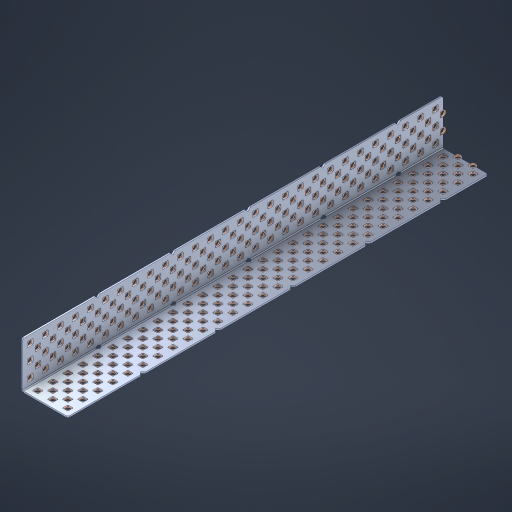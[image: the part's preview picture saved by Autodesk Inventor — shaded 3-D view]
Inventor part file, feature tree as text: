
AUTODESK INVENTOR PART (.ipt)
format: ipt  version: 2023 (Build 270158000, 158)  size: 2,856,960 bytes
history: native  units: in
note: dims shown in document units (in); Inventor stores cm internally (conversion verified against a paired STEP export)
features: other x286, extrude x278, sheet_metal_op x8, sketch x7, pattern_linear x3, mirror x1, chamfer x1
ambient origin geometry x8: Origin, YZ Plane, XZ Plane, XY Plane, X Axis, Y Axis, Z Axis, Center Point
bodies: Solid1 (feature_tree), Body (feature_tree)
feature tree (584):
  sheet_metal_op  "Flanges"
  sheet_metal_op  "Body Pattern"
  pattern_linear  "Center Double"  Spacing1=1.5in  [1 undecoded]
  pattern_linear  "Center Pattern"  Spacing1=0.1875in  [1 undecoded]
  other  "Arc Length"
  pattern_linear  "Notch Pattern"  Spacing1=0.0469in  [1 undecoded]
  other  "Diagonal Plane"
  mirror  "Everything Mirrored"
  chamfer  "End Chamfer"
  sketch  "Sketch1"  dims[d0=1.5in]
  other  "Plate1"
  sketch  "Sketch2"  dims[d1=14.0in]
  other  "Plate2"
  sheet_metal_op  "Bend1"
  sheet_metal_op  "Corner1"
  sketch  "Sketch8"  dims[d2=0.0469in]
  sketch  "Sketch9"  dims[d3=0.0469in]
  other  "Srf91"
  sheet_metal_op  "Body Pattern Sketch"
  other  "Srf92"
  sketch  "Sketch13"  dims[d4=0.0234in]
  sketch  "Sketch15"  dims[d5=0.0938in]
  sketch  "Sketch16"  dims[d6=0.0469in d7=1.5in d8=90.0deg d9=0.0312in d10=0.1875in d11=0.0469in d12=0.0469in d49=0.182in d50=0.02in d52=0.25in d53=0.0469in d54=0.0in d55=0.172in d56=1.0in d57=0.0in d85=0.1473in d86=0.1659in d89=0.0469in d90=0.0in d91=0.04in d92=0.0491in d95=2.5in d96=0.04in d97=0.25in d98=45.0deg d106=0.182in d107=0.02in d110=0.0469in d111=0.0in d112=0.172in d113=0.5in d114=0.0in d117=0.5in d126=0.0491in d127=0.1227in d128=0.08in d129=0.04in d130=2.5in d131=0.25in d132=11.0236in d134=0.5in d135=1.1811in d137=0.5in d140=0.5in d141=1.0in d142=0.3937in d144=0.5in d145=0.071in d146=0.7874in d148=0.5in]
  other  "Srf786"
  other  "Srf856"
  other  "Srf889"
  other  "Srf890"
  other  "Srf891"
  other  "Srf1275"
  other  "Srf1276"
  other  "Srf1278"
  other  "Srf1277"
  other  "Srf1285"
  other  "Srf1286"
  other  "Srf1287"
  other  "Srf1445"
  other  "Srf1446"
  other  "Srf1447"
  other  "Srf1448"
  other  "Srf1449"
  other  "Srf1537"
  other  "Srf1538"
  other  "Srf1539"
  other  "Srf1540"
  other  "Srf1541"
  other  "Srf1807"
  other  "Srf1808"
  other  "Srf1809"
  other  "Srf1810"
  other  "Srf1811"
  other  "Srf1812"
  other  "Srf1813"
  other  "Srf1814"
  other  "Srf1815"
  other  "Srf1816"
  other  "Srf1817"
  other  "Srf1818"
  other  "Srf1819"
  other  "Srf1820"
  other  "Srf1821"
  other  "Srf1822"
  other  "Srf1823"
  other  "Srf1824"
  other  "Srf1825"
  other  "Srf1959"
  other  "Srf1960"
  other  "Srf1961"
  other  "Srf1962"
  other  "Srf1963"
  other  "Srf1964"
  other  "Srf1965"
  other  "Srf1966"
  other  "Srf1967"
  other  "Srf1968"
  other  "Srf1969"
  other  "Srf1970"
  other  "Srf1971"
  other  "Srf1972"
  other  "Srf1973"
  other  "Srf1974"
  other  "Srf1975"
  other  "Srf1976"
  other  "Srf1977"
  other  "Srf2009"
  other  "Srf2010"
  other  "Srf2011"
  other  "Srf2012"
  other  "Srf2013"
  other  "Srf2014"
  other  "Srf2015"
  other  "Srf2016"
  other  "Srf2017"
  other  "Srf2018"
  other  "Srf2019"
  other  "Srf2020"
  other  "Srf2021"
  other  "Srf2022"
  other  "Srf2023"
  other  "Srf2024"
  other  "Srf2025"
  other  "Srf2026"
  other  "Srf2027"
  other  "Srf2028"
  other  "Srf2029"
  other  "Srf2030"
  other  "Srf2031"
  other  "Srf2032"
  other  "Srf2033"
  other  "Srf2034"
  other  "Srf2035"
  other  "Srf2036"
  other  "Srf2043"
  other  "Srf2044"
  other  "Srf2045"
  other  "Srf2046"
  other  "Srf2047"
  other  "Srf2048"
  other  "Srf2049"
  other  "Srf2050"
  other  "Srf2051"
  other  "Srf2052"
  other  "Srf2053"
  other  "Srf2054"
  other  "Srf2055"
  other  "Srf2056"
  other  "Srf2057"
  other  "Srf2058"
  other  "Srf2059"
  other  "Srf2060"
  other  "Srf2061"
  other  "Srf2062"
  other  "Srf2063"
  other  "Srf2064"
  other  "Srf2065"
  other  "Srf2066"
  other  "Srf2067"
  other  "Srf2068"
  other  "Srf2069"
  other  "Srf2076"
  other  "Srf2077"
  other  "Srf2078"
  other  "Srf2079"
  other  "Srf2080"
  other  "Srf2081"
  other  "Srf2082"
  other  "Srf2083"
  other  "Srf2084"
  other  "Srf2085"
  other  "Srf2086"
  other  "Srf2087"
  other  "Srf2088"
  other  "Srf2089"
  other  "Srf2090"
  other  "Srf2091"
  other  "Srf2092"
  other  "Srf2093"
  other  "Srf2094"
  other  "Srf2095"
  other  "Srf2096"
  other  "Srf2097"
  other  "Srf2098"
  other  "Srf2099"
  other  "Srf2100"
  other  "Srf2101"
  other  "Srf2102"
  other  "Srf2103"
  other  "Srf2104"
  other  "Srf2105"
  other  "Srf2106"
  other  "Srf2107"
  other  "Srf2108"
  other  "Srf2109"
  other  "Srf2110"
  other  "Srf2111"
  other  "Srf2112"
  other  "Srf2113"
  other  "Srf2114"
  other  "Srf2115"
  other  "Srf2116"
  other  "Srf2117"
  other  "Srf2118"
  other  "Srf2119"
  other  "Srf2120"
  other  "Srf2121"
  other  "Srf2122"
  other  "Srf2123"
  other  "Srf2124"
  other  "Srf2125"
  other  "Srf2126"
  other  "Srf2127"
  other  "Srf2128"
  other  "Srf2129"
  other  "Srf2130"
  other  "Srf2131"
  other  "Srf2132"
  other  "Srf2133"
  other  "Srf2134"
  other  "Srf2135"
  other  "Srf2136"
  other  "Srf2137"
  other  "Srf2138"
  other  "Srf2139"
  other  "Srf2140"
  other  "Srf2141"
  other  "Srf2142"
  other  "Srf2143"
  other  "Srf2144"
  other  "Srf2145"
  other  "Srf2146"
  other  "Srf2147"
  other  "Srf2148"
  other  "Srf2149"
  other  "Srf2150"
  other  "Srf2151"
  other  "Srf2152"
  other  "Srf2153"
  other  "Srf2154"
  other  "Srf2155"
  other  "Srf2156"
  other  "Srf2157"
  other  "Srf2179"
  other  "Srf2180"
  other  "Srf2181"
  other  "Srf2182"
  other  "Srf2183"
  other  "Srf2184"
  other  "Srf2185"
  other  "Srf2186"
  other  "Srf2187"
  other  "Srf2188"
  other  "Srf2189"
  other  "Srf2190"
  other  "Srf2191"
  other  "Srf2192"
  other  "Srf2193"
  other  "Srf2194"
  other  "Srf2195"
  other  "Srf2196"
  other  "Srf2197"
  other  "Srf2198"
  other  "Srf2199"
  other  "Srf2200"
  other  "Srf2201"
  other  "Srf2202"
  other  "Srf2203"
  other  "Srf2204"
  other  "Srf2205"
  other  "Srf2206"
  other  "Srf2207"
  other  "Srf2208"
  other  "Srf2209"
  other  "Srf2210"
  other  "Srf2211"
  other  "Srf2212"
  other  "Srf2213"
  other  "Srf2214"
  other  "Srf2215"
  other  "Srf2216"
  other  "Srf2217"
  other  "Srf2218"
  other  "Srf2219"
  other  "Srf2220"
  other  "Srf2221"
  other  "Srf2222"
  other  "Srf2223"
  other  "Srf2224"
  other  "Srf2225"
  other  "Srf2226"
  other  "Srf2227"
  other  "Srf2228"
  other  "Srf2229"
  other  "Srf2230"
  other  "Srf2231"
  other  "Srf2232"
  other  "Srf2233"
  other  "Srf2234"
  other  "Srf2235"
  other  "Srf2236"
  other  "Srf2237"
  other  "Srf2238"
  other  "Srf2239"
  other  "Srf2240"
  other  "Srf2241"
  other  "Srf2242"
  other  "Srf2243"
  other  "Srf2244"
  other  "Srf2245"
  other  "Srf2246"
  other  "Srf2247"
  other  "Srf2248"
  other  "Srf2249"
  other  "Srf2250"
  other  "Srf2251"
  other  "Srf2252"
  other  "Srf2253"
  other  "Srf2254"
  other  "Srf2255"
  other  "Srf2256"
  other  "Srf2257"
  other  "Srf2258"
  other  "Srf2259"
  sheet_metal_op  "Body Stamp"
  sheet_metal_op  "Body Circle"
  other  "Center Stamp"
  other  "Center Circle"
  sheet_metal_op  "Notch"
  extrude  "ExtrusionSrf92"  Depth=0.0469in
  extrude  "ExtrusionSrf856"  Depth=0.182in
  extrude  "ExtrusionSrf889"  Depth=0.02in
  extrude  "ExtrusionSrf890"  Depth=0.25in
  extrude  "ExtrusionSrf891"  Depth=0.0469in
  extrude  "ExtrusionSrf1275"  TaperAngle=0.0deg  [1 undecoded]
  extrude  "ExtrusionSrf1276"  Depth=0.5in
  extrude  "ExtrusionSrf1277"  Depth=1.0in TaperAngle=0.0deg
  extrude  "ExtrusionSrf1345"  Depth=0.5in
  extrude  "ExtrusionSrf1346"  Depth=0.5in
  extrude  "ExtrusionSrf1347"  Depth=0.0469in
  extrude  "ExtrusionSrf1348"  Depth=0.5in TaperAngle=0.0deg
  extrude  "ExtrusionSrf1445"  Depth=0.5in
  extrude  "ExtrusionSrf1446"  Depth=0.25in TaperAngle=45.0deg
  extrude  "ExtrusionSrf1447"  Depth=0.182in
  extrude  "ExtrusionSrf1448"  Depth=0.02in
  extrude  "ExtrusionSrf1449"  Depth=0.0469in
  extrude  "ExtrusionSrf1537"  TaperAngle=0.0deg  [1 undecoded]
  extrude  "ExtrusionSrf1538"  Depth=0.5in
  extrude  "ExtrusionSrf1539"  Depth=0.5in TaperAngle=0.0deg
  extrude  "ExtrusionSrf1540"  Depth=0.5in
  extrude  "ExtrusionSrf1541"  Depth=0.5in
  extrude  "ExtrusionSrf1807"  Depth=0.5in
  extrude  "ExtrusionSrf1808"  Depth=0.5in
  extrude  "ExtrusionSrf1809"  Depth=0.5in
  extrude  "ExtrusionSrf1810"  Depth=0.5in
  extrude  "ExtrusionSrf1811"  Depth=0.25in
  extrude  "ExtrusionSrf1812"  Depth=0.5in
  extrude  "ExtrusionSrf1813"  Depth=0.5in
  extrude  "ExtrusionSrf1814"  Depth=0.5in
  extrude  "ExtrusionSrf1815"  Depth=1.0in
  extrude  "ExtrusionSrf1816"  Depth=0.3937in
  extrude  "ExtrusionSrf1817"  Depth=0.5in
  extrude  "ExtrusionSrf1818"  Depth=0.5in
  extrude  "ExtrusionSrf1819"  [1 undecoded]
  extrude  "ExtrusionSrf1820"  [1 undecoded]
  extrude  "ExtrusionSrf1821"  [1 undecoded]
  extrude  "ExtrusionSrf1822"  [1 undecoded]
  extrude  "ExtrusionSrf1823"  [1 undecoded]
  extrude  "ExtrusionSrf1824"  [1 undecoded]
  extrude  "ExtrusionSrf1825"  [1 undecoded]
  extrude  "ExtrusionSrf1959"  [1 undecoded]
  extrude  "ExtrusionSrf1960"  [1 undecoded]
  extrude  "ExtrusionSrf1961"  [1 undecoded]
  extrude  "ExtrusionSrf1962"  [1 undecoded]
  extrude  "ExtrusionSrf1963"  [1 undecoded]
  extrude  "ExtrusionSrf1964"  [1 undecoded]
  extrude  "ExtrusionSrf1965"  [1 undecoded]
  extrude  "ExtrusionSrf1966"  [1 undecoded]
  extrude  "ExtrusionSrf1967"  [1 undecoded]
  extrude  "ExtrusionSrf1968"  [1 undecoded]
  extrude  "ExtrusionSrf1969"  [1 undecoded]
  extrude  "ExtrusionSrf1970"  [1 undecoded]
  extrude  "ExtrusionSrf1971"  [1 undecoded]
  extrude  "ExtrusionSrf1972"  [1 undecoded]
  extrude  "ExtrusionSrf1973"  [1 undecoded]
  extrude  "ExtrusionSrf1974"  [1 undecoded]
  extrude  "ExtrusionSrf1975"  [1 undecoded]
  extrude  "ExtrusionSrf1976"  [1 undecoded]
  extrude  "ExtrusionSrf1977"  [1 undecoded]
  extrude  "ExtrusionSrf2009"  [1 undecoded]
  extrude  "ExtrusionSrf2010"  [1 undecoded]
  extrude  "ExtrusionSrf2011"  [1 undecoded]
  extrude  "ExtrusionSrf2012"  [1 undecoded]
  extrude  "ExtrusionSrf2013"  [1 undecoded]
  extrude  "ExtrusionSrf2014"  [1 undecoded]
  extrude  "ExtrusionSrf2015"  [1 undecoded]
  extrude  "ExtrusionSrf2016"  [1 undecoded]
  extrude  "ExtrusionSrf2017"  [1 undecoded]
  extrude  "ExtrusionSrf2018"  [1 undecoded]
  extrude  "ExtrusionSrf2019"  [1 undecoded]
  extrude  "ExtrusionSrf2020"  [1 undecoded]
  extrude  "ExtrusionSrf2021"  [1 undecoded]
  extrude  "ExtrusionSrf2022"  [1 undecoded]
  extrude  "ExtrusionSrf2023"  [1 undecoded]
  extrude  "ExtrusionSrf2024"  [1 undecoded]
  extrude  "ExtrusionSrf2025"  [1 undecoded]
  extrude  "ExtrusionSrf2026"  [1 undecoded]
  extrude  "ExtrusionSrf2027"  [1 undecoded]
  extrude  "ExtrusionSrf2028"  [1 undecoded]
  extrude  "ExtrusionSrf2029"  [1 undecoded]
  extrude  "ExtrusionSrf2030"  [1 undecoded]
  extrude  "ExtrusionSrf2031"  [1 undecoded]
  extrude  "ExtrusionSrf2032"  [1 undecoded]
  extrude  "ExtrusionSrf2033"  [1 undecoded]
  extrude  "ExtrusionSrf2034"  [1 undecoded]
  extrude  "ExtrusionSrf2035"  [1 undecoded]
  extrude  "ExtrusionSrf2036"  [1 undecoded]
  extrude  "ExtrusionSrf2043"  [1 undecoded]
  extrude  "ExtrusionSrf2044"  [1 undecoded]
  extrude  "ExtrusionSrf2045"  [1 undecoded]
  extrude  "ExtrusionSrf2046"  [1 undecoded]
  extrude  "ExtrusionSrf2047"  [1 undecoded]
  extrude  "ExtrusionSrf2048"  [1 undecoded]
  extrude  "ExtrusionSrf2049"  [1 undecoded]
  extrude  "ExtrusionSrf2050"  [1 undecoded]
  extrude  "ExtrusionSrf2051"  [1 undecoded]
  extrude  "ExtrusionSrf2052"  [1 undecoded]
  extrude  "ExtrusionSrf2053"  [1 undecoded]
  extrude  "ExtrusionSrf2054"  [1 undecoded]
  extrude  "ExtrusionSrf2055"  [1 undecoded]
  extrude  "ExtrusionSrf2056"  [1 undecoded]
  extrude  "ExtrusionSrf2057"  [1 undecoded]
  extrude  "ExtrusionSrf2058"  [1 undecoded]
  extrude  "ExtrusionSrf2059"  [1 undecoded]
  extrude  "ExtrusionSrf2060"  [1 undecoded]
  extrude  "ExtrusionSrf2061"  [1 undecoded]
  extrude  "ExtrusionSrf2062"  [1 undecoded]
  extrude  "ExtrusionSrf2063"  [1 undecoded]
  extrude  "ExtrusionSrf2064"  [1 undecoded]
  extrude  "ExtrusionSrf2065"  [1 undecoded]
  extrude  "ExtrusionSrf2066"  [1 undecoded]
  extrude  "ExtrusionSrf2067"  [1 undecoded]
  extrude  "ExtrusionSrf2068"  [1 undecoded]
  extrude  "ExtrusionSrf2069"  [1 undecoded]
  extrude  "ExtrusionSrf2076"  [1 undecoded]
  extrude  "ExtrusionSrf2077"  [1 undecoded]
  extrude  "ExtrusionSrf2078"  [1 undecoded]
  extrude  "ExtrusionSrf2079"  [1 undecoded]
  extrude  "ExtrusionSrf2080"  [1 undecoded]
  extrude  "ExtrusionSrf2081"  [1 undecoded]
  extrude  "ExtrusionSrf2082"  [1 undecoded]
  extrude  "ExtrusionSrf2083"  [1 undecoded]
  extrude  "ExtrusionSrf2084"  [1 undecoded]
  extrude  "ExtrusionSrf2085"  [1 undecoded]
  extrude  "ExtrusionSrf2086"  [1 undecoded]
  extrude  "ExtrusionSrf2087"  [1 undecoded]
  extrude  "ExtrusionSrf2088"  [1 undecoded]
  extrude  "ExtrusionSrf2089"  [1 undecoded]
  extrude  "ExtrusionSrf2090"  [1 undecoded]
  extrude  "ExtrusionSrf2091"  [1 undecoded]
  extrude  "ExtrusionSrf2092"  [1 undecoded]
  extrude  "ExtrusionSrf2093"  [1 undecoded]
  extrude  "ExtrusionSrf2094"  [1 undecoded]
  extrude  "ExtrusionSrf2095"  [1 undecoded]
  extrude  "ExtrusionSrf2096"  [1 undecoded]
  extrude  "ExtrusionSrf2097"  [1 undecoded]
  extrude  "ExtrusionSrf2098"  [1 undecoded]
  extrude  "ExtrusionSrf2099"  [1 undecoded]
  extrude  "ExtrusionSrf2100"  [1 undecoded]
  extrude  "ExtrusionSrf2101"  [1 undecoded]
  extrude  "ExtrusionSrf2102"  [1 undecoded]
  extrude  "ExtrusionSrf2103"  [1 undecoded]
  extrude  "ExtrusionSrf2104"  [1 undecoded]
  extrude  "ExtrusionSrf2105"  [1 undecoded]
  extrude  "ExtrusionSrf2106"  [1 undecoded]
  extrude  "ExtrusionSrf2107"  [1 undecoded]
  extrude  "ExtrusionSrf2108"  [1 undecoded]
  extrude  "ExtrusionSrf2109"  [1 undecoded]
  extrude  "ExtrusionSrf2110"  [1 undecoded]
  extrude  "ExtrusionSrf2111"  [1 undecoded]
  extrude  "ExtrusionSrf2112"  [1 undecoded]
  extrude  "ExtrusionSrf2113"  [1 undecoded]
  extrude  "ExtrusionSrf2114"  [1 undecoded]
  extrude  "ExtrusionSrf2115"  [1 undecoded]
  extrude  "ExtrusionSrf2116"  [1 undecoded]
  extrude  "ExtrusionSrf2117"  [1 undecoded]
  extrude  "ExtrusionSrf2118"  [1 undecoded]
  extrude  "ExtrusionSrf2119"  [1 undecoded]
  extrude  "ExtrusionSrf2120"  [1 undecoded]
  extrude  "ExtrusionSrf2121"  [1 undecoded]
  extrude  "ExtrusionSrf2122"  [1 undecoded]
  extrude  "ExtrusionSrf2123"  [1 undecoded]
  extrude  "ExtrusionSrf2124"  [1 undecoded]
  extrude  "ExtrusionSrf2125"  [1 undecoded]
  extrude  "ExtrusionSrf2126"  [1 undecoded]
  extrude  "ExtrusionSrf2127"  [1 undecoded]
  extrude  "ExtrusionSrf2128"  [1 undecoded]
  extrude  "ExtrusionSrf2129"  [1 undecoded]
  extrude  "ExtrusionSrf2130"  [1 undecoded]
  extrude  "ExtrusionSrf2131"  [1 undecoded]
  extrude  "ExtrusionSrf2132"  [1 undecoded]
  extrude  "ExtrusionSrf2133"  [1 undecoded]
  extrude  "ExtrusionSrf2134"  [1 undecoded]
  extrude  "ExtrusionSrf2135"  [1 undecoded]
  extrude  "ExtrusionSrf2136"  [1 undecoded]
  extrude  "ExtrusionSrf2137"  [1 undecoded]
  extrude  "ExtrusionSrf2138"  [1 undecoded]
  extrude  "ExtrusionSrf2139"  [1 undecoded]
  extrude  "ExtrusionSrf2140"  [1 undecoded]
  extrude  "ExtrusionSrf2141"  [1 undecoded]
  extrude  "ExtrusionSrf2142"  [1 undecoded]
  extrude  "ExtrusionSrf2143"  [1 undecoded]
  extrude  "ExtrusionSrf2144"  [1 undecoded]
  extrude  "ExtrusionSrf2145"  [1 undecoded]
  extrude  "ExtrusionSrf2146"  [1 undecoded]
  extrude  "ExtrusionSrf2147"  [1 undecoded]
  extrude  "ExtrusionSrf2148"  [1 undecoded]
  extrude  "ExtrusionSrf2149"  [1 undecoded]
  extrude  "ExtrusionSrf2150"  [1 undecoded]
  extrude  "ExtrusionSrf2151"  [1 undecoded]
  extrude  "ExtrusionSrf2152"  [1 undecoded]
  extrude  "ExtrusionSrf2153"  [1 undecoded]
  extrude  "ExtrusionSrf2154"  [1 undecoded]
  extrude  "ExtrusionSrf2155"  [1 undecoded]
  extrude  "ExtrusionSrf2156"  [1 undecoded]
  extrude  "ExtrusionSrf2157"  [1 undecoded]
  extrude  "ExtrusionSrf2179"  [1 undecoded]
  extrude  "ExtrusionSrf2180"  [1 undecoded]
  extrude  "ExtrusionSrf2181"  [1 undecoded]
  extrude  "ExtrusionSrf2182"  [1 undecoded]
  extrude  "ExtrusionSrf2183"  [1 undecoded]
  extrude  "ExtrusionSrf2184"  [1 undecoded]
  extrude  "ExtrusionSrf2185"  [1 undecoded]
  extrude  "ExtrusionSrf2186"  [1 undecoded]
  extrude  "ExtrusionSrf2187"  [1 undecoded]
  extrude  "ExtrusionSrf2188"  [1 undecoded]
  extrude  "ExtrusionSrf2189"  [1 undecoded]
  extrude  "ExtrusionSrf2190"  [1 undecoded]
  extrude  "ExtrusionSrf2191"  [1 undecoded]
  extrude  "ExtrusionSrf2192"  [1 undecoded]
  extrude  "ExtrusionSrf2193"  [1 undecoded]
  extrude  "ExtrusionSrf2194"  [1 undecoded]
  extrude  "ExtrusionSrf2195"  [1 undecoded]
  extrude  "ExtrusionSrf2196"  [1 undecoded]
  extrude  "ExtrusionSrf2197"  [1 undecoded]
  extrude  "ExtrusionSrf2198"  [1 undecoded]
  extrude  "ExtrusionSrf2199"  [1 undecoded]
  extrude  "ExtrusionSrf2200"  [1 undecoded]
  extrude  "ExtrusionSrf2201"  [1 undecoded]
  extrude  "ExtrusionSrf2202"  [1 undecoded]
  extrude  "ExtrusionSrf2203"  [1 undecoded]
  extrude  "ExtrusionSrf2204"  [1 undecoded]
  extrude  "ExtrusionSrf2205"  [1 undecoded]
  extrude  "ExtrusionSrf2206"  [1 undecoded]
  extrude  "ExtrusionSrf2207"  [1 undecoded]
  extrude  "ExtrusionSrf2208"  [1 undecoded]
  extrude  "ExtrusionSrf2209"  [1 undecoded]
  extrude  "ExtrusionSrf2210"  [1 undecoded]
  extrude  "ExtrusionSrf2211"  [1 undecoded]
  extrude  "ExtrusionSrf2212"  [1 undecoded]
  extrude  "ExtrusionSrf2213"  [1 undecoded]
  extrude  "ExtrusionSrf2214"  [1 undecoded]
  extrude  "ExtrusionSrf2215"  [1 undecoded]
  extrude  "ExtrusionSrf2216"  [1 undecoded]
  extrude  "ExtrusionSrf2217"  [1 undecoded]
  extrude  "ExtrusionSrf2218"  [1 undecoded]
  extrude  "ExtrusionSrf2219"  [1 undecoded]
  extrude  "ExtrusionSrf2220"  [1 undecoded]
  extrude  "ExtrusionSrf2221"  [1 undecoded]
  extrude  "ExtrusionSrf2222"  [1 undecoded]
  extrude  "ExtrusionSrf2223"  [1 undecoded]
  extrude  "ExtrusionSrf2224"  [1 undecoded]
  extrude  "ExtrusionSrf2225"  [1 undecoded]
  extrude  "ExtrusionSrf2226"  [1 undecoded]
  extrude  "ExtrusionSrf2227"  [1 undecoded]
  extrude  "ExtrusionSrf2228"  [1 undecoded]
  extrude  "ExtrusionSrf2229"  [1 undecoded]
  extrude  "ExtrusionSrf2230"  [1 undecoded]
  extrude  "ExtrusionSrf2231"  [1 undecoded]
  extrude  "ExtrusionSrf2232"  [1 undecoded]
  extrude  "ExtrusionSrf2233"  [1 undecoded]
  extrude  "ExtrusionSrf2234"  [1 undecoded]
  extrude  "ExtrusionSrf2235"  [1 undecoded]
  extrude  "ExtrusionSrf2236"  [1 undecoded]
  extrude  "ExtrusionSrf2237"  [1 undecoded]
  extrude  "ExtrusionSrf2238"  [1 undecoded]
  extrude  "ExtrusionSrf2239"  [1 undecoded]
  extrude  "ExtrusionSrf2240"  [1 undecoded]
  extrude  "ExtrusionSrf2241"  [1 undecoded]
  extrude  "ExtrusionSrf2242"  [1 undecoded]
  extrude  "ExtrusionSrf2243"  [1 undecoded]
  extrude  "ExtrusionSrf2244"  [1 undecoded]
  extrude  "ExtrusionSrf2245"  [1 undecoded]
  extrude  "ExtrusionSrf2246"  [1 undecoded]
  extrude  "ExtrusionSrf2247"  [1 undecoded]
  extrude  "ExtrusionSrf2248"  [1 undecoded]
  extrude  "ExtrusionSrf2249"  [1 undecoded]
  extrude  "ExtrusionSrf2250"  [1 undecoded]
  extrude  "ExtrusionSrf2251"  [1 undecoded]
  extrude  "ExtrusionSrf2252"  [1 undecoded]
  extrude  "ExtrusionSrf2253"  [1 undecoded]
  extrude  "ExtrusionSrf2254"  [1 undecoded]
  extrude  "ExtrusionSrf2255"  [1 undecoded]
  extrude  "ExtrusionSrf2256"  [1 undecoded]
  extrude  "ExtrusionSrf2257"  [1 undecoded]
  extrude  "ExtrusionSrf2258"  [1 undecoded]
  extrude  "ExtrusionSrf2259"  [1 undecoded]
note: 249 required parameter values undecoded (feature->parameter linkage not recoverable at this tier; creation-order binding heuristic only, values carry confidence <= 0.55)
